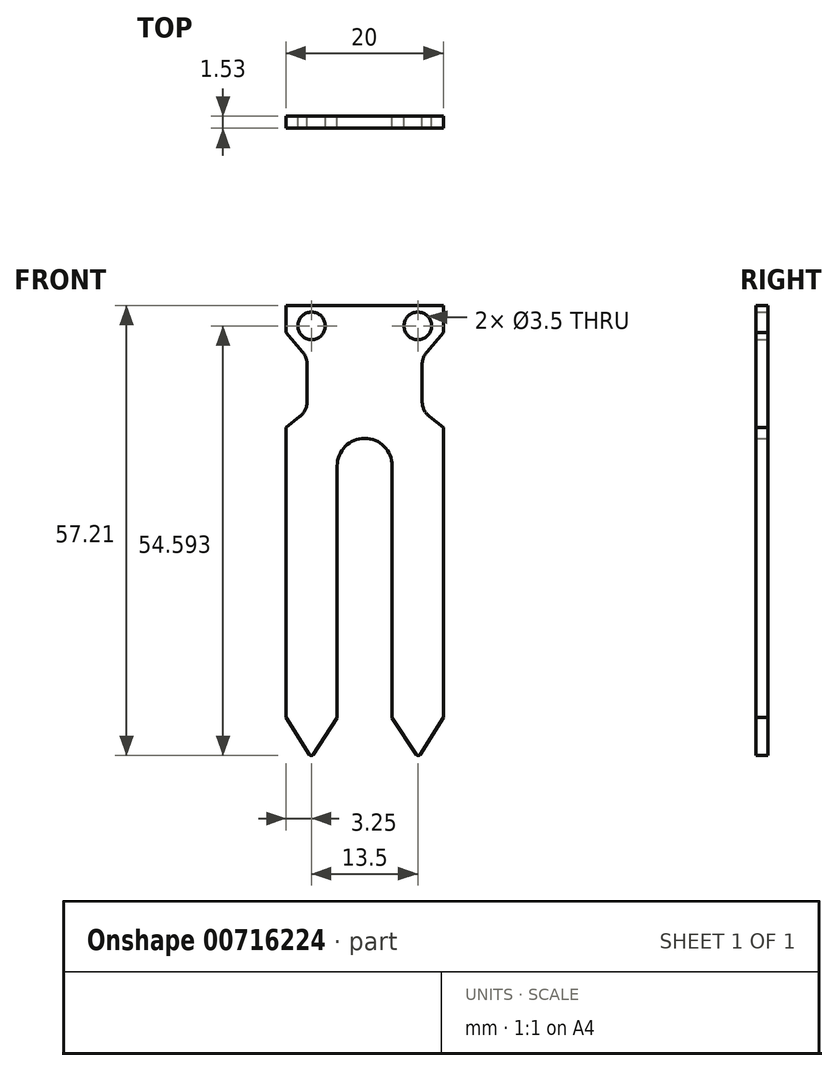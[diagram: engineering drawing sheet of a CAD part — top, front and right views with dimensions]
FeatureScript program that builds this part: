
annotation { "Feature Type Name" : "Feature", "Feature Type Description" : "" }
export const myFeature = defineFeature(function(context is Context, id is Id, definition is map)
    precondition{}
    {
        {
            var Q0;
            Q0=qCreatedBy(makeId("Front.planeOp"),FACE);
            var sketch = newSketch(context, id + "F0", { "sketchPlane" : qUnion([Q0])});
            skLineSegment(sketch, "E0", {"start": v(0, 0) * mm, "end": v(10, 0) * mm});
            skLineSegment(sketch, "E1", {"start": v(10, 0) * mm, "end": v(10, -3.44) * mm});
            skLineSegment(sketch, "E2", {"start": v(10, -3.44) * mm, "end": v(7.3, -6.62) * mm});
            skLineSegment(sketch, "E3", {"start": v(7.3, -6.62) * mm, "end": v(7.3, -13.4) * mm});
            skLineSegment(sketch, "E4", {"start": v(7.3, -13.4) * mm, "end": v(10, -15.54) * mm});
            skLineSegment(sketch, "E5", {"start": v(10, -15.54) * mm, "end": v(10, -52.35) * mm});
            skLineSegment(sketch, "E6", {"start": v(6.79, -57.42) * mm, "end": v(3.5, -52.4) * mm});
            skLineSegment(sketch, "E7", {"start": v(3.5, -52.4) * mm, "end": v(3.5, -20.4) * mm});
            skArc(sketch, "E8", {"start": v(3.5, -20.4) * mm, "mid": v(2.47, -17.93) * mm, "end": v(0, -16.9) * mm});
            skLineSegment(sketch, "E9.MirrorCS", {"start": v(0, 0) * mm, "end": v(-10, 0) * mm});
            skLineSegment(sketch, "E10.MirrorCS", {"start": v(-10, -3.44) * mm, "end": v(-7.3, -6.62) * mm});
            skLineSegment(sketch, "E11.MirrorCS", {"start": v(-7.3, -6.62) * mm, "end": v(-7.3, -13.4) * mm});
            skLineSegment(sketch, "E12.MirrorCS", {"start": v(-7.3, -13.4) * mm, "end": v(-10, -15.54) * mm});
            skLineSegment(sketch, "E13.MirrorCS", {"start": v(-10, -15.54) * mm, "end": v(-10, -52.35) * mm});
            skLineSegment(sketch, "E14.MirrorCS", {"start": v(-6.79, -57.42) * mm, "end": v(-3.5, -52.4) * mm});
            skLineSegment(sketch, "E15.MirrorCS", {"start": v(-3.5, -52.4) * mm, "end": v(-3.5, -20.4) * mm});
            skArc(sketch, "E16.MirrorCS", {"start": v(-3.5, -20.4) * mm, "mid": v(-2.47, -17.93) * mm, "end": v(0, -16.9) * mm});
            skLineSegment(sketch, "E17", {"start": v(-10, 0) * mm, "end": v(-10, -3.44) * mm});
            skCircle(sketch, "E18", {"center": v(-6.75, -2.62) * mm, "radius": 1.75 * mm});
            skCircle(sketch, "E19.MirrorC", {"center": v(6.75, -2.62) * mm, "radius": 1.75 * mm});
            skLineSegment(sketch, "E20", {"start": v(10, -52.35) * mm, "end": v(6.79, -57.42) * mm});
            skLineSegment(sketch, "E21", {"start": v(-6.79, -57.42) * mm, "end": v(-10, -52.35) * mm});
            skSolve(sketch);
        }
        {
            var Q0;
            Q0 = qSketchRegion(id + "F0", true);
            extrude(context, id + "F1", {"entities" : qUnion([Q0]), "depth" : 1.53 * mm, "offsetDistance" : 25 * mm});
        }
        {
            var Q0;
            Q0=makeQuery(id+"F1.opExtrude","SWEPT_EDGE",EDGE,{"disambiguationData":[OSD([sQuery(id+"F0.wireOp",EDGE,"E14.MirrorCS"),sQuery(id+"F0.wireOp",EDGE,"E21")])]});
            var Q1;
            Q1=makeQuery(id+"F1.opExtrude","SWEPT_EDGE",EDGE,{"disambiguationData":[OSD([sQuery(id+"F0.wireOp",EDGE,"E6"),sQuery(id+"F0.wireOp",EDGE,"E20")])]});
            fillet(context, id + "F2", {"entities" : qUnion([Q0, Q1]), "radius" : .25 * mm, "tangentPropagation" : true, "allowEdgeOverflow" : false});
        }
        {
            var Q0;
            Q0=makeQuery(id+"F1.opExtrude","SWEPT_EDGE",EDGE,{"disambiguationData":[OSD([sQuery(id+"F0.wireOp",EDGE,"E11.MirrorCS"),sQuery(id+"F0.wireOp",EDGE,"E12.MirrorCS")])]});
            var Q1;
            Q1=makeQuery(id+"F1.opExtrude","SWEPT_EDGE",EDGE,{"disambiguationData":[OSD([sQuery(id+"F0.wireOp",EDGE,"E10.MirrorCS"),sQuery(id+"F0.wireOp",EDGE,"E11.MirrorCS")])]});
            var Q2;
            Q2=makeQuery(id+"F1.opExtrude","SWEPT_EDGE",EDGE,{"disambiguationData":[OSD([sQuery(id+"F0.wireOp",EDGE,"E2"),sQuery(id+"F0.wireOp",EDGE,"E3")])]});
            var Q3;
            Q3=makeQuery(id+"F1.opExtrude","SWEPT_EDGE",EDGE,{"disambiguationData":[OSD([sQuery(id+"F0.wireOp",EDGE,"E3"),sQuery(id+"F0.wireOp",EDGE,"E4")])]});
            fillet(context, id + "F3", {"entities" : qUnion([Q0, Q1, Q2, Q3]), "radius" : 2.5 * mm, "tangentPropagation" : true, "allowEdgeOverflow" : false});
        }
    });
